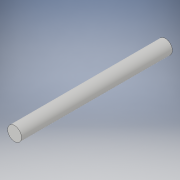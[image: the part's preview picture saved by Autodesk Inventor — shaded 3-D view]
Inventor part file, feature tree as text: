
AUTODESK INVENTOR PART (.ipt)
format: ipt  version: 2017 (Build 210142000, 142)  size: 89,088 bytes
history: native  units: in
note: dims shown in document units (in); Inventor stores cm internally (conversion verified against a paired STEP export)
features: extrude x1, sketch x1
ambient origin geometry x8: Origin, YZ Plane, XZ Plane, XY Plane, X Axis, Y Axis, Z Axis, Center Point
bodies: Solid1 (feature_tree)
feature tree (2):
  extrude  "Extrusion1"  Depth=1.49in TaperAngle=0.0deg
  sketch  "Sketch1"  dims[d0=0.138in d1=1.49in d2=0.0in]
